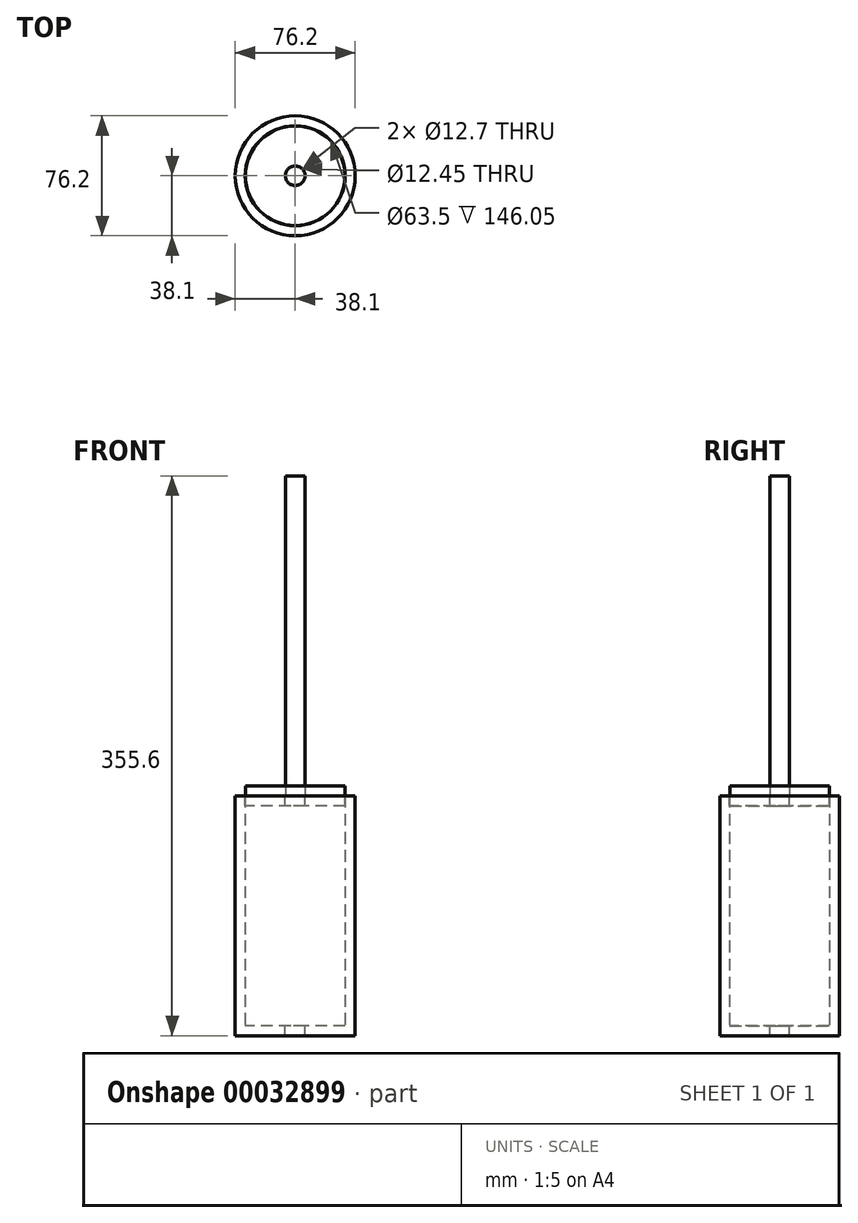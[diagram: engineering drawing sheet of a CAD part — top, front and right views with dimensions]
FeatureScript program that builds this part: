
annotation { "Feature Type Name" : "Feature", "Feature Type Description" : "" }
export const myFeature = defineFeature(function(context is Context, id is Id, definition is map)
    precondition{}
    {
        {
            var Q0;
            Q0=qCreatedBy(makeId("Top.planeOp"),FACE);
            var sketch = newSketch(context, id + "F0", { "sketchPlane" : qUnion([Q0])});
            skCircle(sketch, "E0", {"center": v(0, 0) * mm, "radius": 38.1 * mm});
            skSolve(sketch);
        }
        {
            var Q0;
            Q0=makeQuery(id+"F0.imprint","IMPRINT",FACE,{"disambiguationData":[TD([[makeQuery(id+"F0.imprint","IMPRINT",EDGE,{"derivedFrom":sQuery(id+"F0.wireOp",EDGE,"E0")}),1.0]])]});
            extrude(context, id + "F1", {"entities" : qUnion([Q0]), "endBound" : BoundingType.SYMMETRIC, "depth" : 152.4 * mm});
        }
        {
            var Q0;
            Q0=makeQuery(id+"F1.opExtrude","CAP_FACE",FACE,{"disambiguationData":[OSD([sQuery(id+"F0.wireOp",EDGE,"E0")])],"isStart":false});
            shell(context, id + "F2", {"entities" : qUnion([Q0]), "thickness" : 6.35 * mm});
        }
        {
            var Q0;
            Q0=makeQuery(id+"F1.opExtrude","CAP_FACE",FACE,{"disambiguationData":[OSD([sQuery(id+"F0.wireOp",EDGE,"E0")])],"isStart":false});
            var sketch = newSketch(context, id + "F3", { "sketchPlane" : qUnion([Q0])});
            skCircle(sketch, "E1.0", {"center": v(0, 0) * mm, "radius": 31.75 * mm});
            skSolve(sketch);
        }
        {
            var Q0;
            Q0=makeQuery(id+"F3.imprint","IMPRINT",FACE,{"disambiguationData":[TD([[makeQuery(id+"F3.imprint","IMPRINT",EDGE,{"derivedFrom":sQuery(id+"F3.wireOp",EDGE,"E1.0")}),1.0]])]});
            extrude(context, id + "F4", {"entities" : qUnion([Q0]), "oppositeDirection" : true, "depth" : 6.35 * mm});
        }
        {
            var Q0;
            Q0=makeQuery(id+"F4.opExtrude","CAP_FACE",FACE,{"disambiguationData":[OSD([sQuery(id+"F3.wireOp",EDGE,"E1.0")])],"isStart":true});
            var sketch = newSketch(context, id + "F5", { "sketchPlane" : qUnion([Q0])});
            skCircle(sketch, "E2.0.0", {"center": v(0, 0) * mm, "radius": 31.75 * mm});
            skCircle(sketch, "E3", {"center": v(0, 0) * mm, "radius": 6.35 * mm});
            skSolve(sketch);
        }
        {
            var Q0;
            Q0=makeQuery(id+"F5.imprint","IMPRINT",FACE,{"disambiguationData":[TD([[makeQuery(id+"F5.imprint","IMPRINT",EDGE,{"derivedFrom":sQuery(id+"F5.wireOp",EDGE,"E3")}),1.0]])]});
            extrude(context, id + "F6", {"entities" : qUnion([Q0]), "operationType" : NewBodyOperationType.REMOVE, "endBound" : BoundingType.THROUGH_ALL, "oppositeDirection" : true, "depth" : 25.4 * mm});
        }
        {
            var Q0;
            Q0=makeQuery(id+"F4.opExtrude","CAP_FACE",FACE,{"disambiguationData":[OSD([sQuery(id+"F3.wireOp",EDGE,"E1.0")])],"isStart":true});
            var sketch = newSketch(context, id + "F7", { "sketchPlane" : qUnion([Q0])});
            skCircle(sketch, "E4.0", {"center": v(0, 0) * mm, "radius": 6.35 * mm});
            skCircle(sketch, "E5", {"center": v(0, 0) * mm, "radius": 6.22 * mm});
            skSolve(sketch);
        }
        {
            var Q0;
            Q0=makeQuery(id+"F7.imprint","IMPRINT",FACE,{"disambiguationData":[TD([[makeQuery(id+"F7.imprint","IMPRINT",EDGE,{"derivedFrom":sQuery(id+"F7.wireOp",EDGE,"E5")}),1.0]])]});
            extrude(context, id + "F8", {"entities" : qUnion([Q0]), "depth" : 203.2 * mm});
        }
        {
            var Q0;
            Q0=makeQuery(id+"F8.opExtrude","CAP_FACE",FACE,{"disambiguationData":[OSD([sQuery(id+"F7.wireOp",EDGE,"E5")])],"isStart":true});
            var sketch = newSketch(context, id + "F9", { "sketchPlane" : qUnion([Q0])});
            skCircle(sketch, "E6", {"center": v(0, 0) * mm, "radius": 31.62 * mm});
            skCircle(sketch, "E7.0", {"center": v(0, 0) * mm, "radius": 31.75 * mm});
            skSolve(sketch);
        }
        {
            var Q0;
            Q0=makeQuery(id+"F9.imprint","IMPRINT",FACE,{"disambiguationData":[TD([[makeQuery(id+"F9.imprint","IMPRINT",EDGE,{"derivedFrom":sQuery(id+"F9.wireOp",EDGE,"E6")}),1.0]])]});
            extrude(context, id + "F10", {"entities" : qUnion([Q0]), "oppositeDirection" : true, "depth" : 6.35 * mm});
        }
    });
